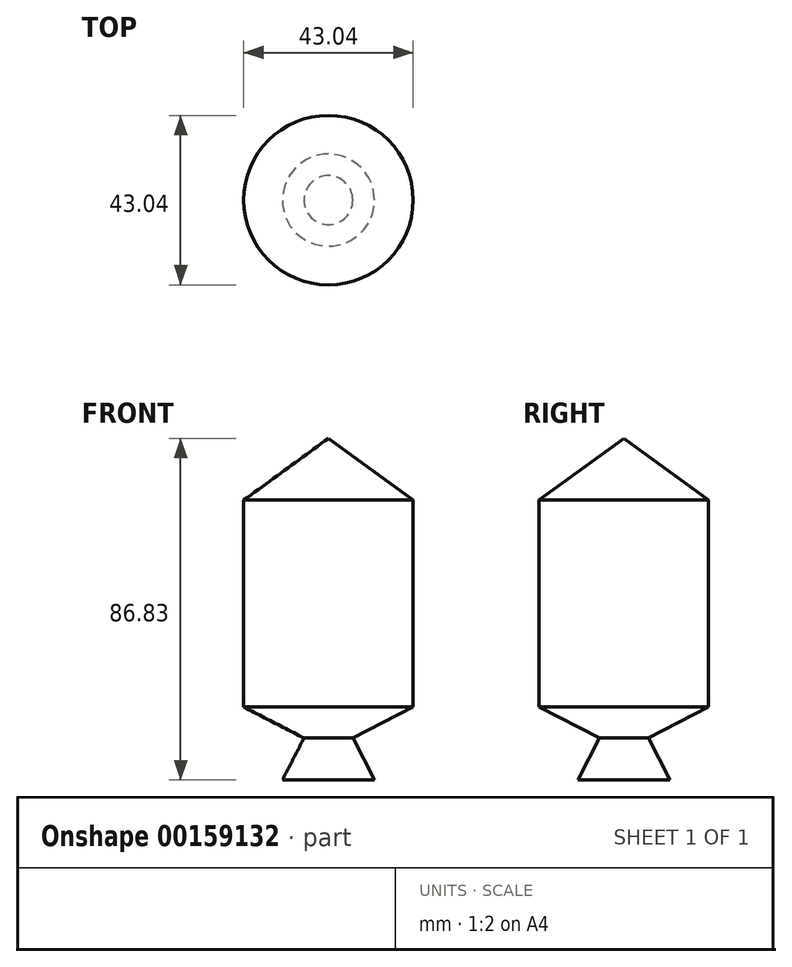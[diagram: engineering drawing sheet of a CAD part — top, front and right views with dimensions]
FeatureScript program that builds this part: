
annotation { "Feature Type Name" : "Feature", "Feature Type Description" : "" }
export const myFeature = defineFeature(function(context is Context, id is Id, definition is map)
    precondition{}
    {
        {
            var Q0;
            Q0=qCreatedBy(makeId("Front.planeOp"),FACE);
            var sketch = newSketch(context, id + "F0", { "sketchPlane" : qUnion([Q0])});
            skLineSegment(sketch, "E0", {"start": v(0, 59.38) * mm, "end": v(-21.52, 43.66) * mm});
            skLineSegment(sketch, "E1", {"start": v(-21.52, 43.66) * mm, "end": v(-21.52, -8.9) * mm});
            skLineSegment(sketch, "E2", {"start": v(-21.52, -8.9) * mm, "end": v(-6.2, -16.76) * mm});
            skLineSegment(sketch, "E3", {"start": v(-6.2, -16.76) * mm, "end": v(-11.7, -27.45) * mm});
            skLineSegment(sketch, "E4", {"start": v(-11.7, -27.45) * mm, "end": v(0, -27.45) * mm});
            skLineSegment(sketch, "E5", {"start": v(0, -27.45) * mm, "end": v(0, 59.38) * mm});
            skSolve(sketch);
        }
        {
            var Q0;
            Q0=makeQuery(id+"F0.imprint","IMPRINT",FACE,{"disambiguationData":[TD([[makeQuery(id+"F0.imprint","IMPRINT",EDGE,{"derivedFrom":sQuery(id+"F0.wireOp",EDGE,"E0")}),1.0]])]});
            var Q1;
            Q1=sQuery(id+"F0.wireOp",EDGE,"E5");
            revolve(context, id + "F1", {"entities" : qUnion([Q0]), "axis" : qUnion([Q1]), "revolveType" : RevolveType.FULL});
        }
    });
